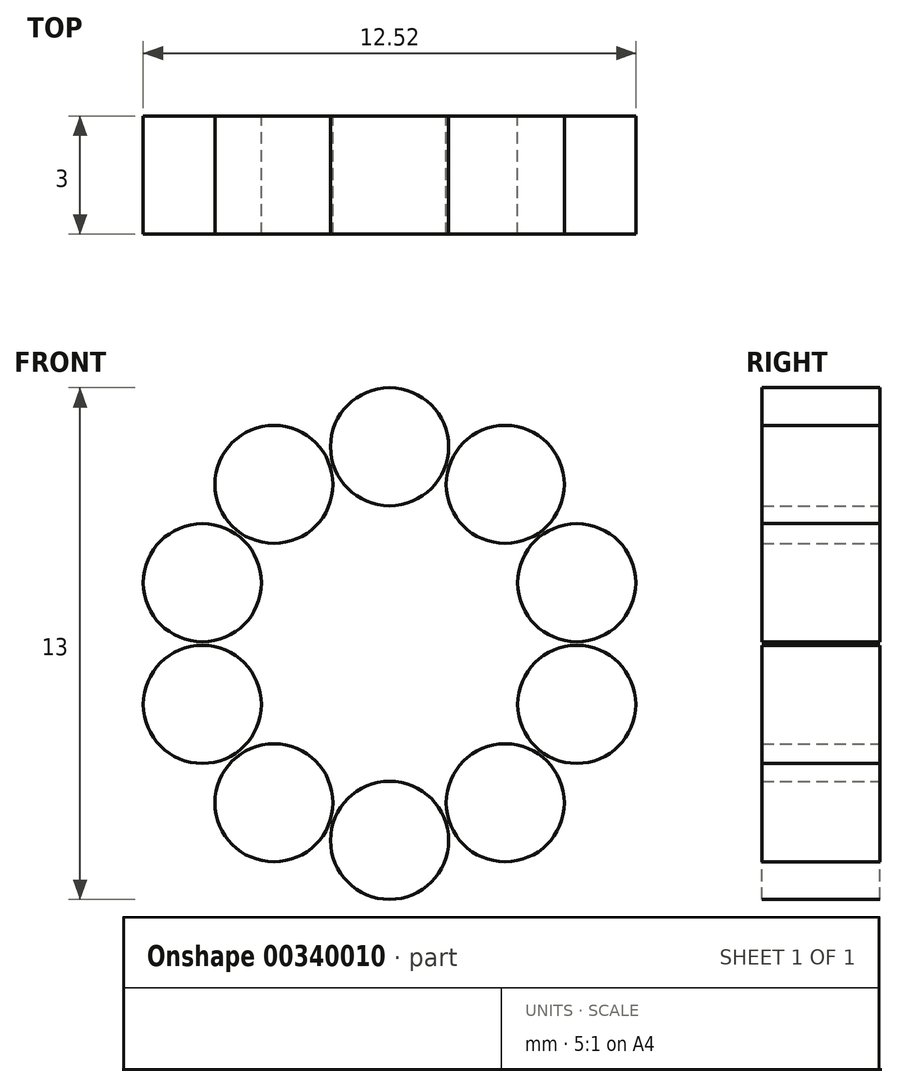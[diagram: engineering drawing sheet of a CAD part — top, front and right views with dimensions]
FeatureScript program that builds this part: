
annotation { "Feature Type Name" : "Feature", "Feature Type Description" : "" }
export const myFeature = defineFeature(function(context is Context, id is Id, definition is map)
    precondition{}
    {
        {
            var Q0;
            Q0=qCreatedBy(makeId("Front.planeOp"),FACE);
            var sketch = newSketch(context, id + "F0", { "sketchPlane" : qUnion([Q0])});
            skCircle(sketch, "E0", {"center": v(0, -5) * mm, "radius": 1.5 * mm});
            skCircle(sketch, "E1", {"center": v(0, 0) * mm, "radius": 5 * mm, "construction": true});
            skCircle(sketch, "E2.1.0", {"center": v(2.94, -4.05) * mm, "radius": 1.5 * mm});
            skCircle(sketch, "E2.2.0", {"center": v(4.76, -1.55) * mm, "radius": 1.5 * mm});
            skCircle(sketch, "E2.3.0", {"center": v(4.76, 1.55) * mm, "radius": 1.5 * mm});
            skCircle(sketch, "E2.4.0", {"center": v(2.94, 4.05) * mm, "radius": 1.5 * mm});
            skCircle(sketch, "E2.5.0", {"center": v(0, 5) * mm, "radius": 1.5 * mm});
            skCircle(sketch, "E2.6.0", {"center": v(-2.94, 4.05) * mm, "radius": 1.5 * mm});
            skCircle(sketch, "E2.7.0", {"center": v(-4.76, 1.55) * mm, "radius": 1.5 * mm});
            skCircle(sketch, "E2.8.0", {"center": v(-4.76, -1.55) * mm, "radius": 1.5 * mm});
            skCircle(sketch, "E2.9.0", {"center": v(-2.94, -4.05) * mm, "radius": 1.5 * mm});
            skSolve(sketch);
        }
        {
            var Q0;
            Q0 = qSketchRegion(id + "F0", true);
            extrude(context, id + "F1", {"entities" : qUnion([Q0]), "depth" : 3 * mm});
        }
    });
